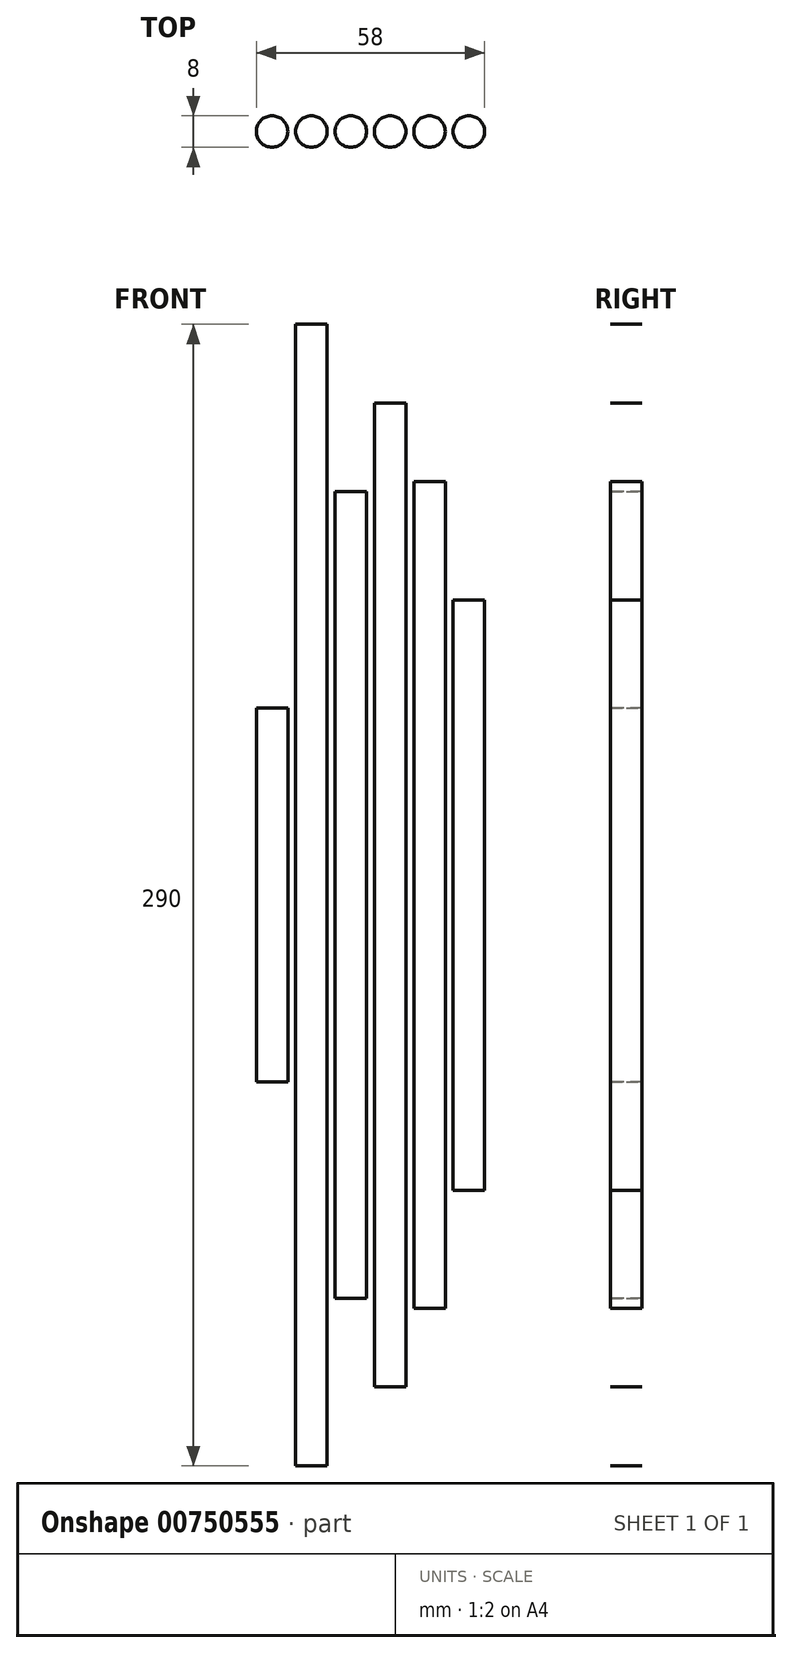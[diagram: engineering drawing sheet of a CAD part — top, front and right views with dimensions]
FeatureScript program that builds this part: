
annotation { "Feature Type Name" : "Feature", "Feature Type Description" : "" }
export const myFeature = defineFeature(function(context is Context, id is Id, definition is map)
    precondition{}
    {
        {
            var Q0;
            Q0=qCreatedBy(makeId("Top.planeOp"),FACE);
            var sketch = newSketch(context, id + "F0", { "sketchPlane" : qUnion([Q0])});
            skCircle(sketch, "E0", {"center": v(0, 0) * mm, "radius": 4 * mm});
            skSolve(sketch);
        }
        {
            var Q0;
            Q0=qSketchRegion(id+"F0",true);
            extrude(context, id + "F1", {"entities" : qUnion([Q0]), "endBound" : BoundingType.SYMMETRIC, "depth" : 210 * mm});
        }
        {
            var Q0;
            Q0=qCreatedBy(makeId("Top.planeOp"),FACE);
            var sketch = newSketch(context, id + "F2", { "sketchPlane" : qUnion([Q0])});
            skCircle(sketch, "E1", {"center": v(10, 0) * mm, "radius": 4 * mm});
            skSolve(sketch);
        }
        {
            var Q0;
            Q0=makeQuery(id+"F2.imprint","IMPRINT",FACE,{"disambiguationData":[TD([[makeQuery(id+"F2.imprint","IMPRINT",EDGE,{"derivedFrom":sQuery(id+"F2.wireOp",EDGE,"E1")}),1.0]])]});
            extrude(context, id + "F3", {"entities" : qUnion([Q0]), "endBound" : BoundingType.SYMMETRIC, "depth" : 150 * mm});
        }
        {
            var Q0;
            Q0=qCreatedBy(makeId("Top.planeOp"),FACE);
            var sketch = newSketch(context, id + "F4", { "sketchPlane" : qUnion([Q0])});
            skCircle(sketch, "E2", {"center": v(-10, 0) * mm, "radius": 4 * mm});
            skSolve(sketch);
        }
        {
            var Q0;
            Q0=makeQuery(id+"F4.imprint","IMPRINT",FACE,{"disambiguationData":[TD([[makeQuery(id+"F4.imprint","IMPRINT",EDGE,{"derivedFrom":sQuery(id+"F4.wireOp",EDGE,"E2")}),1.0]])]});
            extrude(context, id + "F5", {"entities" : qUnion([Q0]), "endBound" : BoundingType.SYMMETRIC, "depth" : 250 * mm});
        }
        {
            var Q0;
            Q0=qCreatedBy(makeId("Top.planeOp"),FACE);
            var sketch = newSketch(context, id + "F6", { "sketchPlane" : qUnion([Q0])});
            skCircle(sketch, "E3", {"center": v(-20, 0) * mm, "radius": 4 * mm});
            skSolve(sketch);
        }
        {
            var Q0;
            Q0=qSketchRegion(id+"F6",true);
            extrude(context, id + "F7", {"entities" : qUnion([Q0]), "endBound" : BoundingType.SYMMETRIC, "depth" : 205 * mm});
        }
        {
            var Q0;
            Q0=qCreatedBy(makeId("Top.planeOp"),FACE);
            var sketch = newSketch(context, id + "F8", { "sketchPlane" : qUnion([Q0])});
            skCircle(sketch, "E4", {"center": v(-30, 0) * mm, "radius": 4 * mm});
            skSolve(sketch);
        }
        {
            var Q0;
            Q0=qSketchRegion(id+"F8",true);
            extrude(context, id + "F9", {"entities" : qUnion([Q0]), "endBound" : BoundingType.SYMMETRIC, "depth" : 290 * mm});
        }
        {
            var Q0;
            Q0=qCreatedBy(makeId("Top.planeOp"),FACE);
            var sketch = newSketch(context, id + "F10", { "sketchPlane" : qUnion([Q0])});
            skCircle(sketch, "E5", {"center": v(-40, 0) * mm, "radius": 4 * mm});
            skSolve(sketch);
        }
        {
            var Q0;
            Q0=qSketchRegion(id+"F10",true);
            extrude(context, id + "F11", {"entities" : qUnion([Q0]), "endBound" : BoundingType.SYMMETRIC, "depth" : 95 * mm});
        }
    });
